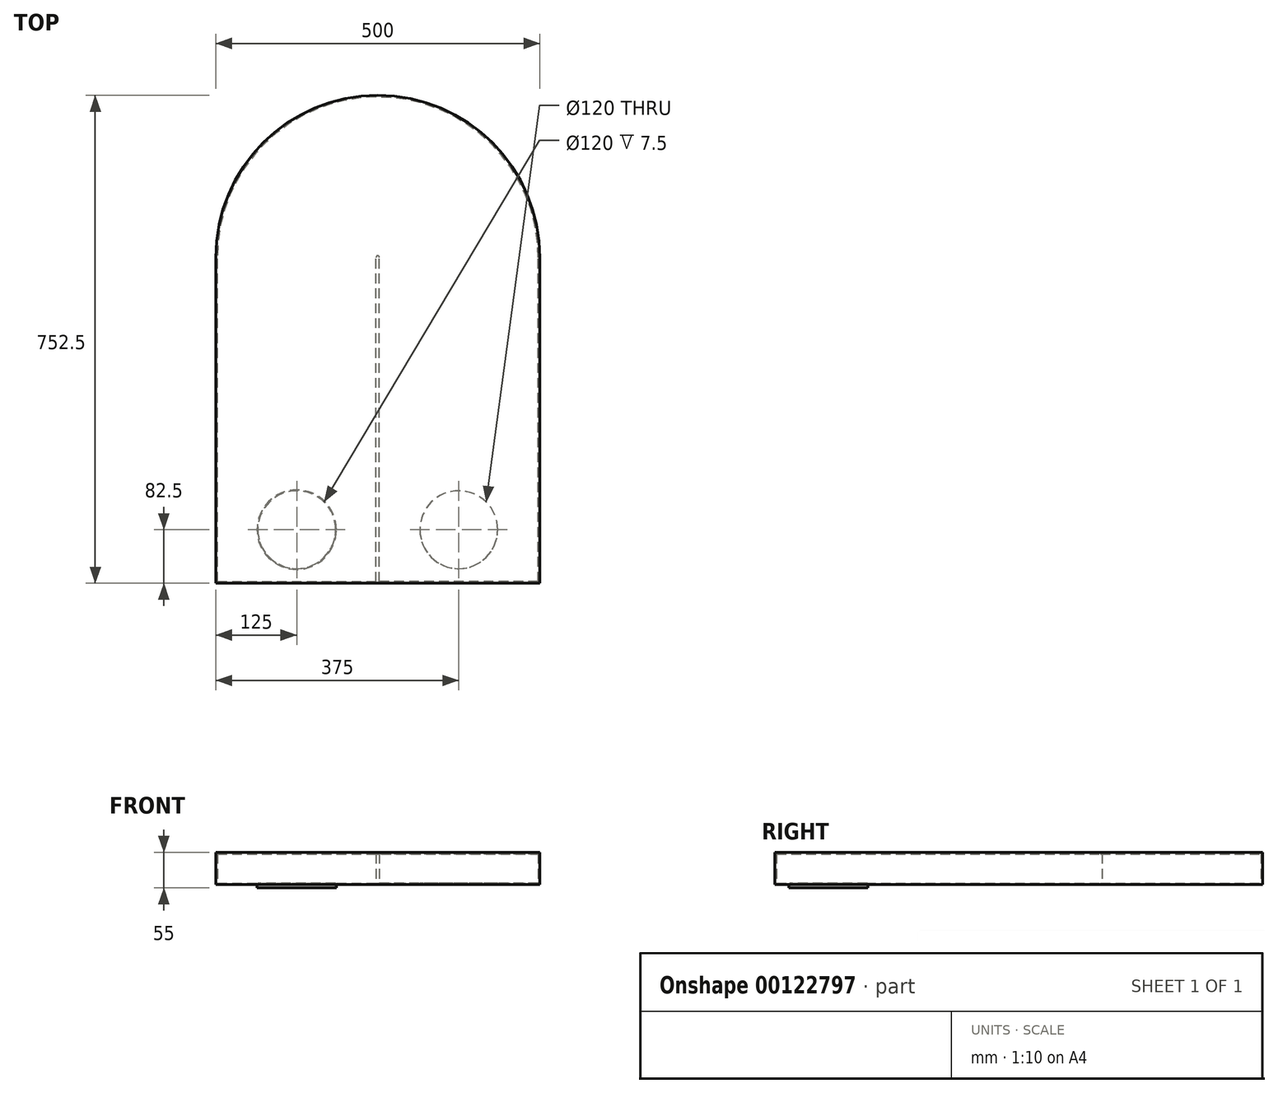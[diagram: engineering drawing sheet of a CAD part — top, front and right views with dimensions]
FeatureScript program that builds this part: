
annotation { "Feature Type Name" : "Feature", "Feature Type Description" : "" }
export const myFeature = defineFeature(function(context is Context, id is Id, definition is map)
    precondition{}
    {
        {
            var Q0;
            Q0=qCreatedBy(makeId("Front.planeOp"),FACE);
            var sketch = newSketch(context, id + "F0", { "sketchPlane" : qUnion([Q0])});
            skLineSegment(sketch, "E0.bottom", {"start": v(-125, 25) * mm, "end": v(125, 25) * mm});
            skLineSegment(sketch, "E0.top", {"start": v(-125, -25) * mm, "end": v(125, -25) * mm});
            skLineSegment(sketch, "E0.left", {"start": v(-125, 25) * mm, "end": v(-125, -25) * mm});
            skLineSegment(sketch, "E0.right", {"start": v(125, 25) * mm, "end": v(125, -25) * mm});
            skPoint(sketch, "E0.middle", {"position": v(0, 0) * mm});
            skLineSegment(sketch, "E1.bottom", {"start": v(-122.5, 22.5) * mm, "end": v(122.5, 22.5) * mm});
            skLineSegment(sketch, "E1.top", {"start": v(-122.5, -22.5) * mm, "end": v(122.5, -22.5) * mm});
            skLineSegment(sketch, "E1.left", {"start": v(-122.5, 22.5) * mm, "end": v(-122.5, -22.5) * mm});
            skLineSegment(sketch, "E1.right", {"start": v(122.5, 22.5) * mm, "end": v(122.5, -22.5) * mm});
            skSolve(sketch);
        }
        {
            var Q0;
            Q0=qCreatedBy(makeId("Top.planeOp"),FACE);
            var sketch = newSketch(context, id + "F1", { "sketchPlane" : qUnion([Q0])});
            skLineSegment(sketch, "E2", {"start": v(0, 0) * mm, "end": v(0, -500) * mm});
            skArc(sketch, "E3", {"start": v(250, 0) * mm, "mid": v(125, 125) * mm, "end": v(0, 0) * mm});
            skLineSegment(sketch, "E4", {"start": v(250, 0) * mm, "end": v(250, -500) * mm});
            skSolve(sketch);
        }
        {
            var Q0;
            Q0=makeQuery(id+"F0.imprint","IMPRINT",FACE,{"disambiguationData":[TD([[makeQuery(id+"F0.imprint","IMPRINT",EDGE,{"derivedFrom":sQuery(id+"F0.wireOp",EDGE,"E0.bottom")}),-1.0]])]});
            var Q1;
            Q1=sQuery(id+"F1.wireOp",EDGE,"E3");
            sweep(context, id + "F2", {"profiles" : qUnion([Q0]), "path" : qUnion([Q1])});
        }
        {
            var Q0;
            Q0=makeQuery(id+"F2.opSweep","CAP_FACE",FACE,{"disambiguationData":[OSD([sQuery(id+"F0.wireOp",EDGE,"E0.bottom"),sQuery(id+"F0.wireOp",EDGE,"E0.top"),sQuery(id+"F0.wireOp",EDGE,"E0.left"),sQuery(id+"F0.wireOp",EDGE,"E0.right"),sQuery(id+"F0.wireOp",EDGE,"E1.bottom"),sQuery(id+"F0.wireOp",EDGE,"E1.top"),sQuery(id+"F0.wireOp",EDGE,"E1.left"),sQuery(id+"F0.wireOp",EDGE,"E1.right"),sQuery(id+"F1.wireOp",VERTEX,"E3.start")])],"isStart":false});
            extrude(context, id + "F3", {"entities" : qUnion([Q0]), "operationType" : NewBodyOperationType.ADD, "depth" : 500 * mm});
        }
        {
            var Q0;
            Q0=makeQuery(id+"F3.opExtrude","CAP_FACE",FACE,{"disambiguationData":[OSD([sQuery(id+"F0.wireOp",EDGE,"E0.bottom"),sQuery(id+"F0.wireOp",EDGE,"E0.top"),sQuery(id+"F0.wireOp",EDGE,"E0.left"),sQuery(id+"F0.wireOp",EDGE,"E0.right"),sQuery(id+"F0.wireOp",EDGE,"E1.bottom"),sQuery(id+"F0.wireOp",EDGE,"E1.top"),sQuery(id+"F0.wireOp",EDGE,"E1.left"),sQuery(id+"F0.wireOp",EDGE,"E1.right"),sQuery(id+"F1.wireOp",VERTEX,"E3.start")])],"isStart":false});
            var sketch = newSketch(context, id + "F4", { "sketchPlane" : qUnion([Q0])});
            skLineSegment(sketch, "E5.bottom", {"start": v(-125, -25) * mm, "end": v(375, -25) * mm});
            skLineSegment(sketch, "E5.top", {"start": v(-125, 25) * mm, "end": v(375, 25) * mm});
            skLineSegment(sketch, "E5.left", {"start": v(-125, -25) * mm, "end": v(-125, 25) * mm});
            skLineSegment(sketch, "E5.right", {"start": v(375, -25) * mm, "end": v(375, 25) * mm});
            skSolve(sketch);
        }
        {
            var Q0;
            Q0 = qSketchRegion(id + "F4", true);
            extrude(context, id + "F5", {"entities" : qUnion([Q0]), "operationType" : NewBodyOperationType.ADD, "depth" : 2.5 * mm});
        }
        {
            var Q0;
            {var subQ0=sQuery(id+"F0.wireOp",EDGE,"E1.top");Q0=makeQuery(id+"F3.boolean.opBoolean","MERGE",FACE,{"derivedFrom":[makeQuery(id+"F2.opSweep","SWEPT_FACE",FACE,{"disambiguationData":[OSD([subQ0,sQuery(id+"F1.wireOp",EDGE,"E3")])]}),makeQuery(id+"F3.opExtrude","SWEPT_FACE",FACE,{"disambiguationData":[OSD([subQ0,sQuery(id+"F1.wireOp",VERTEX,"E3.start")])]}),makeQuery(id+"F3.opExtrude","SWEPT_FACE",FACE,{"disambiguationData":[OSD([subQ0,sQuery(id+"F1.wireOp",VERTEX,"E3.end")])]})]});}
            var sketch = newSketch(context, id + "F6", { "sketchPlane" : qUnion([Q0])});
            skPoint(sketch, "E6", {"position": v(0, -420) * mm});
            skPoint(sketch, "E7.1.0.0", {"position": v(250, -420) * mm});
            skLineSegment(sketch, "E7.direction1", {"start": v(0, -420) * mm, "end": v(250, -420) * mm, "construction": true});
            skSolve(sketch);
        }
        {
            var Q0;
            Q0=sQuery(id+"F6.wireOp",VERTEX,"E6");
            var Q1;
            Q1=sQuery(id+"F6.wireOp",VERTEX,"E7.1.0.0");
            var Q2;
            Q2=makeQuery(id+"F2.opSweep","SWEPT_BODY",BODY,{"disambiguationData":[OSD([sQuery(id+"F0.wireOp",EDGE,"E0.bottom"),sQuery(id+"F0.wireOp",EDGE,"E0.top"),sQuery(id+"F0.wireOp",EDGE,"E0.left"),sQuery(id+"F0.wireOp",EDGE,"E0.right"),sQuery(id+"F0.wireOp",EDGE,"E1.bottom"),sQuery(id+"F0.wireOp",EDGE,"E1.top"),sQuery(id+"F0.wireOp",EDGE,"E1.left"),sQuery(id+"F0.wireOp",EDGE,"E1.right"),sQuery(id+"F1.wireOp",EDGE,"E3")])]});
            hole(context, id + "F7", {"style" : HoleStyle.SIMPLE, "endStyle" : HoleEndStyle.THROUGH, "holeDiameter" : 120 * mm, "locations" : qUnion([Q0, Q1]), "scope" : qUnion([Q2]), "isTappedThrough" : true});
        }
        {
            var Q0;
            {var subQ0=sQuery(id+"F0.wireOp",EDGE,"E0.top");Q0=makeQuery(id+"F5.boolean.opBoolean","MERGE",FACE,{"derivedFrom":[makeQuery(id+"F3.boolean.opBoolean","MERGE",FACE,{"derivedFrom":[makeQuery(id+"F2.opSweep","SWEPT_FACE",FACE,{"disambiguationData":[OSD([subQ0,sQuery(id+"F1.wireOp",EDGE,"E3")])]}),makeQuery(id+"F3.opExtrude","SWEPT_FACE",FACE,{"disambiguationData":[OSD([subQ0,sQuery(id+"F1.wireOp",VERTEX,"E3.start")])]})]}),makeQuery(id+"F5.opExtrude","SWEPT_FACE",FACE,{"disambiguationData":[OSD([sQuery(id+"F4.wireOp",EDGE,"E5.bottom")])]})]});}
            var sketch = newSketch(context, id + "F8", { "sketchPlane" : qUnion([Q0])});
            skCircle(sketch, "E8", {"center": v(0, 420) * mm, "radius": 61.25 * mm});
            skCircle(sketch, "E9", {"center": v(250, 420) * mm, "radius": 61.25 * mm});
            skSolve(sketch);
        }
        {
            var Q0;
            Q0=makeQuery(id+"F8.imprint","IMPRINT",FACE,{"disambiguationData":[TD([[makeQuery(id+"F8.imprint","IMPRINT",EDGE,{"derivedFrom":sQuery(id+"F8.wireOp",EDGE,"E8")}),1.0]])]});
            extrude(context, id + "F9", {"entities" : qUnion([Q0]), "operationType" : NewBodyOperationType.ADD, "depth" : 5 * mm});
        }
    });
